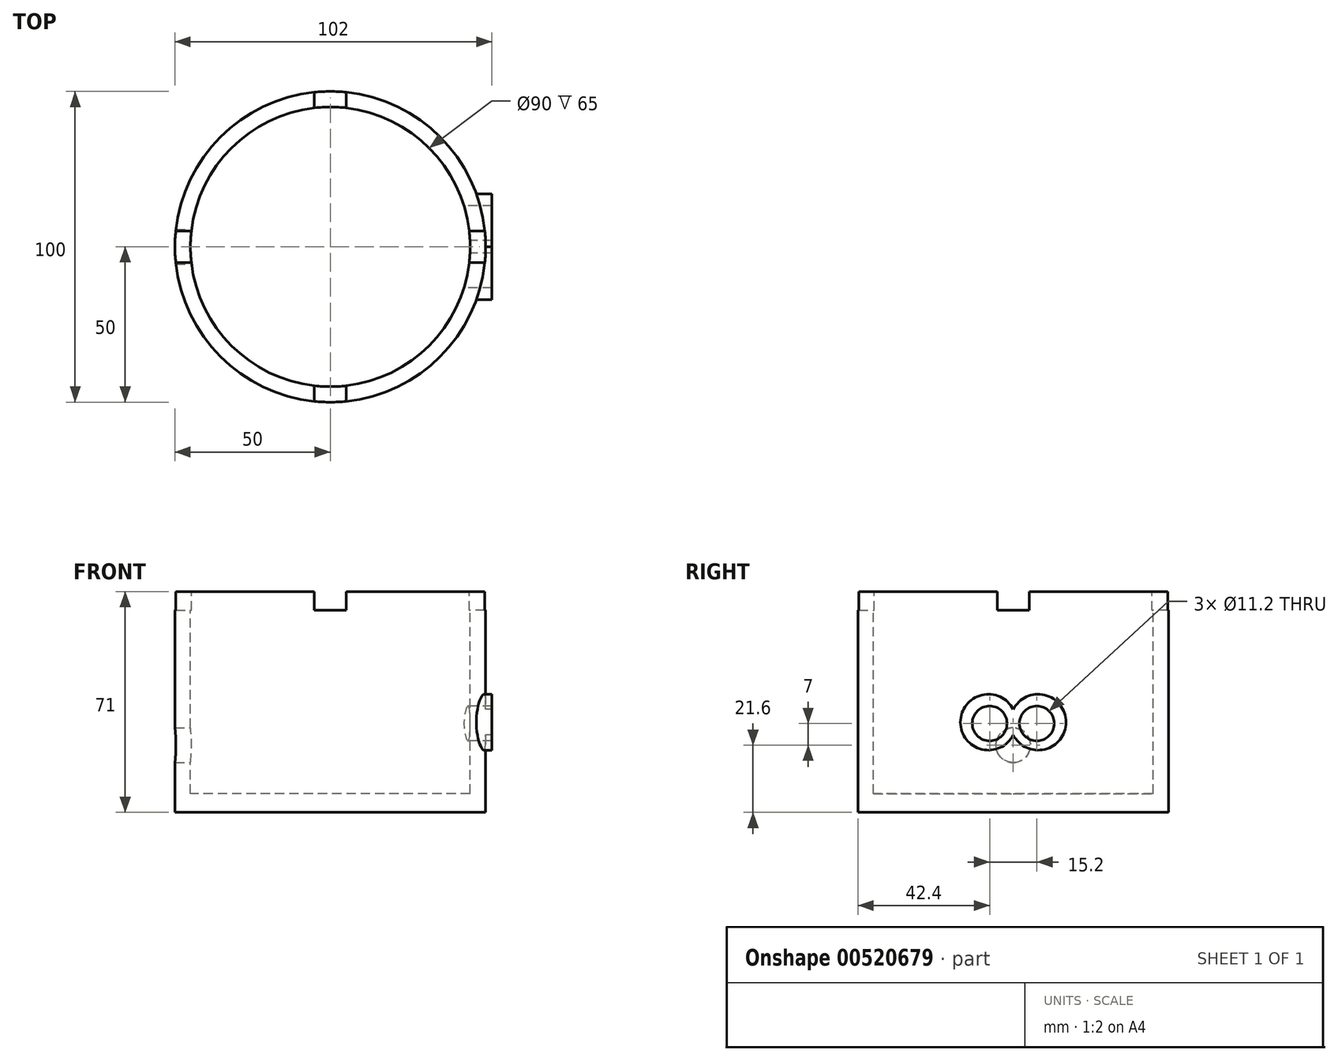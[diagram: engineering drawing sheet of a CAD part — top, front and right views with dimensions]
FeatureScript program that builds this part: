
annotation { "Feature Type Name" : "Feature", "Feature Type Description" : "" }
export const myFeature = defineFeature(function(context is Context, id is Id, definition is map)
    precondition{}
    {
        {
            var Q0;
            Q0=qCreatedBy(makeId("Top.planeOp"),FACE);
            var sketch = newSketch(context, id + "F0", { "sketchPlane" : qUnion([Q0])});
            skCircle(sketch, "E0", {"center": v(0, 0) * mm, "radius": 50 * mm});
            skSolve(sketch);
        }
        {
            var Q0;
            Q0=qSketchRegion(id+"F0",true);
            extrude(context, id + "F1", {"entities" : qUnion([Q0]), "depth" : 71 * mm, "offsetDistance" : 25 * mm});
        }
        {
            var Q0;
            Q0=makeQuery(id+"F1.opExtrude","CAP_FACE",FACE,{"disambiguationData":[OSD([sQuery(id+"F0.wireOp",EDGE,"E0")])],"isStart":false});
            var sketch = newSketch(context, id + "F2", { "sketchPlane" : qUnion([Q0])});
            skCircle(sketch, "E1", {"center": v(0, 0) * mm, "radius": 45 * mm});
            skSolve(sketch);
        }
        {
            var Q0;
            Q0=qSketchRegion(id+"F2",true);
            extrude(context, id + "F3", {"entities" : qUnion([Q0]), "operationType" : NewBodyOperationType.REMOVE, "oppositeDirection" : true, "depth" : 65 * mm, "offsetDistance" : 25 * mm});
        }
        {
            var Q0;
            Q0=qCreatedBy(makeId("Front.planeOp"),FACE);
            var sketch = newSketch(context, id + "F4", { "sketchPlane" : qUnion([Q0])});
            skLineSegment(sketch, "E2.bottom", {"start": v(5.1, 71) * mm, "end": v(-5.1, 71) * mm});
            skLineSegment(sketch, "E2.top", {"start": v(5.1, 65) * mm, "end": v(-5.1, 65) * mm});
            skLineSegment(sketch, "E2.left", {"start": v(5.1, 71) * mm, "end": v(5.1, 65) * mm});
            skLineSegment(sketch, "E2.right", {"start": v(-5.1, 71) * mm, "end": v(-5.1, 65) * mm});
            skSolve(sketch);
        }
        {
            var Q0;
            Q0=qSketchRegion(id+"F4",true);
            extrude(context, id + "F5", {"entities" : qUnion([Q0]), "operationType" : NewBodyOperationType.REMOVE, "oppositeDirection" : true, "depth" : 50 * mm, "offsetDistance" : 25 * mm});
        }
        {
            var Q0;
            Q0=qCreatedBy(makeId("Front.planeOp"),FACE);
            var sketch = newSketch(context, id + "F6", { "sketchPlane" : qUnion([Q0])});
            skLineSegment(sketch, "E3.bottom", {"start": v(5.1, 71) * mm, "end": v(-5.1, 71) * mm});
            skLineSegment(sketch, "E3.top", {"start": v(5.1, 65) * mm, "end": v(-5.1, 65) * mm});
            skLineSegment(sketch, "E3.left", {"start": v(5.1, 71) * mm, "end": v(5.1, 65) * mm});
            skLineSegment(sketch, "E3.right", {"start": v(-5.1, 71) * mm, "end": v(-5.1, 65) * mm});
            skSolve(sketch);
        }
        {
            var Q0;
            Q0=qSketchRegion(id+"F6",true);
            extrude(context, id + "F7", {"entities" : qUnion([Q0]), "operationType" : NewBodyOperationType.REMOVE, "depth" : 50 * mm, "offsetDistance" : 25 * mm});
        }
        {
            var Q0;
            Q0=qCreatedBy(makeId("Right.planeOp"),FACE);
            var sketch = newSketch(context, id + "F8", { "sketchPlane" : qUnion([Q0])});
            skLineSegment(sketch, "E4.bottom", {"start": v(5.1, 71) * mm, "end": v(-5.1, 71) * mm});
            skLineSegment(sketch, "E4.top", {"start": v(5.1, 65) * mm, "end": v(-5.1, 65) * mm});
            skLineSegment(sketch, "E4.left", {"start": v(5.1, 71) * mm, "end": v(5.1, 65) * mm});
            skLineSegment(sketch, "E4.right", {"start": v(-5.1, 71) * mm, "end": v(-5.1, 65) * mm});
            skSolve(sketch);
        }
        {
            var Q0;
            Q0=qSketchRegion(id+"F8",true);
            extrude(context, id + "F9", {"entities" : qUnion([Q0]), "operationType" : NewBodyOperationType.REMOVE, "oppositeDirection" : true, "depth" : 50 * mm, "offsetDistance" : 25 * mm});
        }
        {
            var Q0;
            Q0=qCreatedBy(makeId("Right.planeOp"),FACE);
            var sketch = newSketch(context, id + "F10", { "sketchPlane" : qUnion([Q0])});
            skLineSegment(sketch, "E5.bottom", {"start": v(5.1, 71) * mm, "end": v(-5.1, 71) * mm});
            skLineSegment(sketch, "E5.top", {"start": v(5.1, 65) * mm, "end": v(-5.1, 65) * mm});
            skLineSegment(sketch, "E5.left", {"start": v(5.1, 71) * mm, "end": v(5.1, 65) * mm});
            skLineSegment(sketch, "E5.right", {"start": v(-5.1, 71) * mm, "end": v(-5.1, 65) * mm});
            skSolve(sketch);
        }
        {
            var Q0;
            Q0=qSketchRegion(id+"F10",true);
            extrude(context, id + "F11", {"entities" : qUnion([Q0]), "operationType" : NewBodyOperationType.REMOVE, "depth" : 50 * mm, "offsetDistance" : 25 * mm});
        }
        {
            var Q0;
            Q0=qCreatedBy(makeId("Right.planeOp"),FACE);
            var sketch = newSketch(context, id + "F12", { "sketchPlane" : qUnion([Q0])});
            skCircle(sketch, "E6", {"center": v(0, 21.6) * mm, "radius": 5.6 * mm});
            skSolve(sketch);
        }
        {
            var Q0;
            Q0=qSketchRegion(id+"F12",true);
            extrude(context, id + "F13", {"entities" : qUnion([Q0]), "operationType" : NewBodyOperationType.REMOVE, "oppositeDirection" : true, "depth" : 55 * mm, "offsetDistance" : 25 * mm});
        }
        {
            var Q0;
            Q0=qCreatedBy(makeId("Right.planeOp"),FACE);
            var sketch = newSketch(context, id + "F14", { "sketchPlane" : qUnion([Q0])});
            skCircle(sketch, "E7", {"center": v(-7.6, 28.6) * mm, "radius": 5.6 * mm});
            skCircle(sketch, "E8", {"center": v(7.6, 28.6) * mm, "radius": 5.6 * mm});
            skSolve(sketch);
        }
        {
            var Q0;
            Q0=qSketchRegion(id+"F14",true);
            extrude(context, id + "F15", {"entities" : qUnion([Q0]), "operationType" : NewBodyOperationType.REMOVE, "depth" : 56 * mm, "offsetDistance" : 25 * mm});
        }
        {
            var Q0;
            Q0=qCreatedBy(makeId("Right.planeOp"),FACE);
            var sketch = newSketch(context, id + "F16", { "sketchPlane" : qUnion([Q0])});
            skCircle(sketch, "E9", {"center": v(-8, 29) * mm, "radius": 9 * mm});
            skCircle(sketch, "E10", {"center": v(8, 29) * mm, "radius": 9 * mm});
            skSolve(sketch);
        }
        {
            var Q0;
            Q0 = qSketchRegion(id + "F16", true);
            extrude(context, id + "F17", {"entities" : qUnion([Q0]), "operationType" : NewBodyOperationType.ADD, "depth" : 52 * mm, "offsetDistance" : 25 * mm});
        }
        {
            var Q0;
            Q0 = qSketchRegion(id + "F14", true);
            extrude(context, id + "F18", {"entities" : qUnion([Q0]), "operationType" : NewBodyOperationType.REMOVE, "depth" : 55 * mm, "offsetDistance" : 25 * mm});
        }
        {
            var Q0;
            Q0=makeQuery(id+"F3.boolean.opBoolean","COPY",FACE,{"derivedFrom":makeQuery(id+"F3.opExtrude","CAP_FACE",FACE,{"disambiguationData":[OSD([sQuery(id+"F2.wireOp",EDGE,"E1")])],"isStart":false})});
            var sketch = newSketch(context, id + "F19", { "sketchPlane" : qUnion([Q0])});
            skCircle(sketch, "E11", {"center": v(0, 0) * mm, "radius": 45 * mm});
            skSolve(sketch);
        }
        {
            var Q0;
            Q0 = qSketchRegion(id + "F19", true);
            extrude(context, id + "F20", {"entities" : qUnion([Q0]), "operationType" : NewBodyOperationType.REMOVE, "depth" : 50 * mm, "offsetDistance" : 25 * mm});
        }
    });
